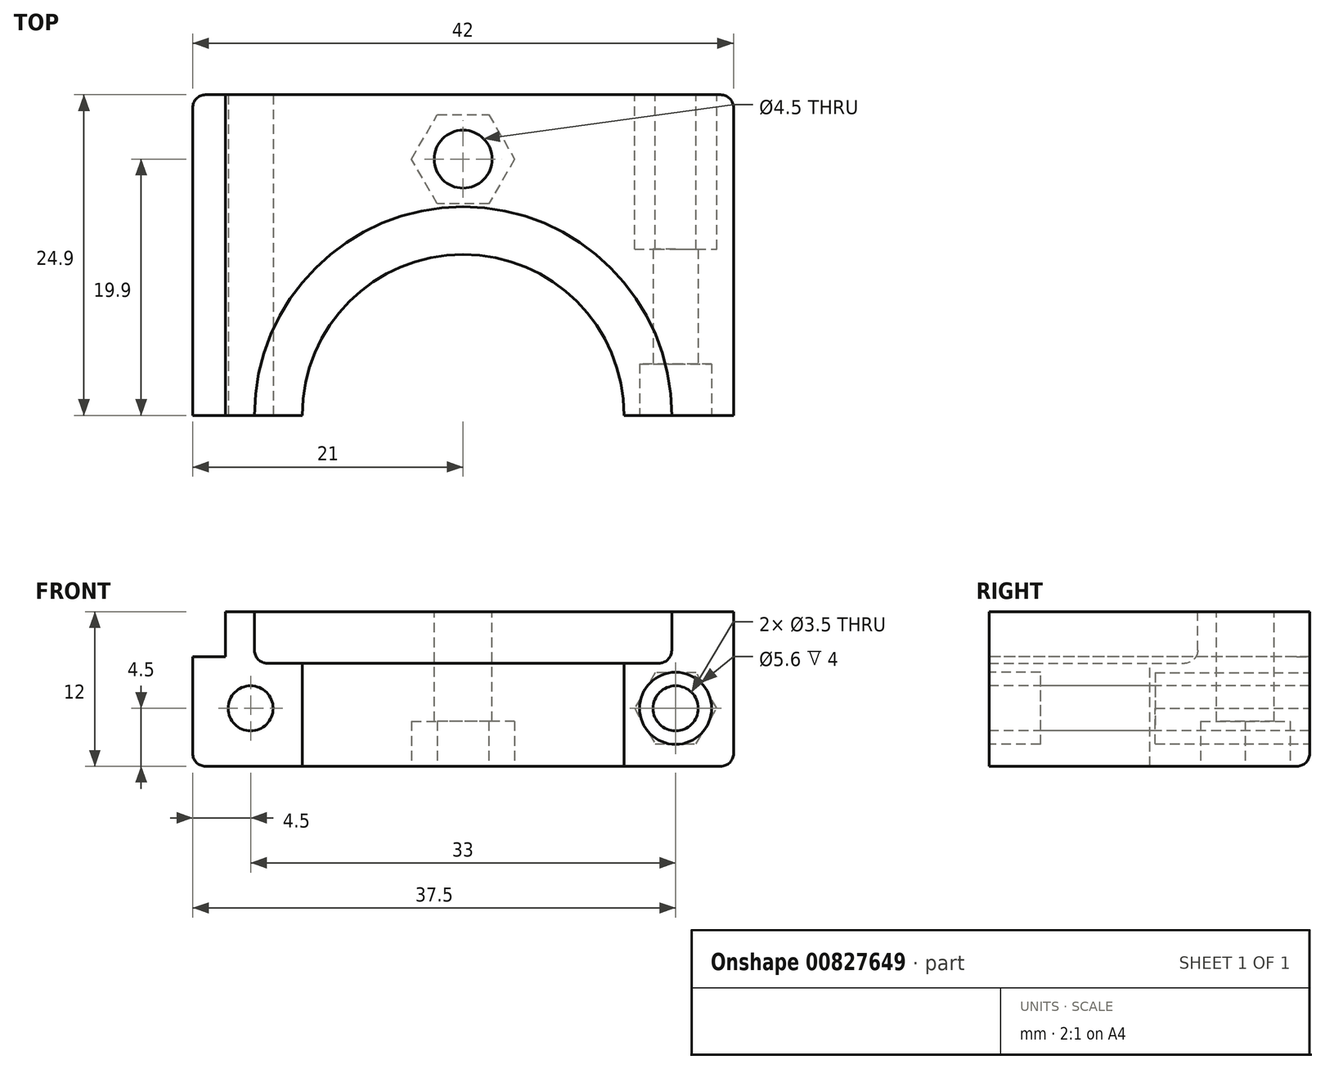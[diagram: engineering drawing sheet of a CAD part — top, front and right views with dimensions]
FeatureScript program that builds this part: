
annotation { "Feature Type Name" : "Feature", "Feature Type Description" : "" }
export const myFeature = defineFeature(function(context is Context, id is Id, definition is map)
    precondition{}
    {
        {
            var Q0;
            Q0=qCreatedBy(makeId("Top.planeOp"),FACE);
            var sketch = newSketch(context, id + "F0", { "sketchPlane" : qUnion([Q0])});
            skLineSegment(sketch, "E0.bottom", {"start": v(-21, 0) * mm, "end": v(21, 0) * mm});
            skLineSegment(sketch, "E0.top", {"start": v(-21, 24.9) * mm, "end": v(21, 24.9) * mm});
            skLineSegment(sketch, "E0.left", {"start": v(-21, 0) * mm, "end": v(-21, 24.9) * mm});
            skLineSegment(sketch, "E0.right", {"start": v(21, 0) * mm, "end": v(21, 24.9) * mm});
            skSolve(sketch);
        }
        {
            var Q0;
            Q0=makeQuery(id+"F0.imprint","IMPRINT",FACE,{"disambiguationData":[TD([[makeQuery(id+"F0.imprint","IMPRINT",EDGE,{"derivedFrom":sQuery(id+"F0.wireOp",EDGE,"E0.bottom")}),1.0]])]});
            extrude(context, id + "F1", {"entities" : qUnion([Q0]), "depth" : 12 * mm, "offsetDistance" : 25 * mm});
        }
        {
            var Q0;
            Q0=makeQuery(id+"F1.opExtrude","CAP_FACE",FACE,{"disambiguationData":[OSD([sQuery(id+"F0.wireOp",EDGE,"E0.bottom"),sQuery(id+"F0.wireOp",EDGE,"E0.top"),sQuery(id+"F0.wireOp",EDGE,"E0.left"),sQuery(id+"F0.wireOp",EDGE,"E0.right")])],"isStart":false});
            var sketch = newSketch(context, id + "F2", { "sketchPlane" : qUnion([Q0])});
            skArc(sketch, "E1", {"start": v(16.2, 0) * mm, "mid": v(0, 16.2) * mm, "end": v(-16.2, 0) * mm});
            skLineSegment(sketch, "E2", {"start": v(-16.2, 0) * mm, "end": v(16.2, 0) * mm});
            skSolve(sketch);
        }
        {
            var Q0;
            Q0=makeQuery(id+"F2.imprint","IMPRINT",FACE,{"disambiguationData":[TD([[makeQuery(id+"F2.imprint","IMPRINT",EDGE,{"derivedFrom":sQuery(id+"F2.wireOp",EDGE,"E1")}),1.0]])]});
            extrude(context, id + "F3", {"entities" : qUnion([Q0]), "operationType" : NewBodyOperationType.REMOVE, "oppositeDirection" : true, "depth" : 4 * mm, "offsetDistance" : 25 * mm});
        }
        {
            var Q0;
            Q0=makeQuery(id+"F3.boolean.opBoolean","COPY",FACE,{"derivedFrom":makeQuery(id+"F3.opExtrude","CAP_FACE",FACE,{"disambiguationData":[OSD([sQuery(id+"F2.wireOp",EDGE,"E1"),sQuery(id+"F2.wireOp",EDGE,"E2")])],"isStart":false})});
            var sketch = newSketch(context, id + "F4", { "sketchPlane" : qUnion([Q0])});
            skArc(sketch, "E3", {"start": v(12.5, 0) * mm, "mid": v(0, 12.5) * mm, "end": v(-12.5, 0) * mm});
            skLineSegment(sketch, "E4", {"start": v(-12.5, 0) * mm, "end": v(12.5, 0) * mm});
            skSolve(sketch);
        }
        {
            var Q0;
            Q0=makeQuery(id+"F4.imprint","IMPRINT",FACE,{"disambiguationData":[TD([[makeQuery(id+"F4.imprint","IMPRINT",EDGE,{"derivedFrom":sQuery(id+"F4.wireOp",EDGE,"E3")}),1.0]])]});
            extrude(context, id + "F5", {"entities" : qUnion([Q0]), "operationType" : NewBodyOperationType.REMOVE, "endBound" : BoundingType.UP_TO_NEXT, "oppositeDirection" : true, "depth" : 25 * mm, "offsetDistance" : 25 * mm});
        }
        {
            var Q0;
            Q0=makeQuery(id+"F1.opExtrude","CAP_FACE",FACE,{"disambiguationData":[OSD([sQuery(id+"F0.wireOp",EDGE,"E0.bottom"),sQuery(id+"F0.wireOp",EDGE,"E0.top"),sQuery(id+"F0.wireOp",EDGE,"E0.left"),sQuery(id+"F0.wireOp",EDGE,"E0.right")])],"isStart":false});
            var sketch = newSketch(context, id + "F6", { "sketchPlane" : qUnion([Q0])});
            skPoint(sketch, "E5", {"position": v(0, 19.9) * mm});
            skSolve(sketch);
        }
        {
            var Q0;
            Q0=sQuery(id+"F6.wireOp",VERTEX,"E5");
            var Q1;
            Q1=makeQuery(id+"F1.opExtrude","SWEPT_BODY",BODY,{"disambiguationData":[OSD([sQuery(id+"F0.wireOp",EDGE,"E0.bottom"),sQuery(id+"F0.wireOp",EDGE,"E0.top"),sQuery(id+"F0.wireOp",EDGE,"E0.left"),sQuery(id+"F0.wireOp",EDGE,"E0.right")])]});
            hole(context, id + "F7", {"style" : HoleStyle.SIMPLE, "endStyle" : HoleEndStyle.THROUGH, "holeDiameter" : 4.5 * mm, "majorDiameter" : 4 * mm, "isTappedThrough" : true, "tappedDepth" : 12 * mm, "tapClearance" : 3, "locations" : qUnion([Q0]), "scope" : qUnion([Q1])});
        }
        {
            var Q0;
            {var subQ1=sQuery(id+"F0.wireOp",EDGE,"E0.left");var subQ4=sQuery(id+"F0.wireOp",EDGE,"E0.bottom");Q0=makeQuery(id+"F5.boolean.opBoolean","SPLIT",FACE,{"disambiguationData":[TD([makeQuery(id+"F1.opExtrude","SWEPT_FACE",FACE,{"disambiguationData":[OSD([subQ1])]})])],"derivedFrom":makeQuery(id+"F1.opExtrude","SWEPT_FACE",FACE,{"disambiguationData":[OSD([subQ4])]})});}
            var sketch = newSketch(context, id + "F8", { "sketchPlane" : qUnion([Q0])});
            skLineSegment(sketch, "E6.bottom", {"start": v(-21, 12) * mm, "end": v(-18.45, 12) * mm});
            skLineSegment(sketch, "E6.top", {"start": v(-21, 8.5) * mm, "end": v(-18.45, 8.5) * mm});
            skLineSegment(sketch, "E6.left", {"start": v(-21, 12) * mm, "end": v(-21, 8.5) * mm});
            skLineSegment(sketch, "E6.right", {"start": v(-18.45, 12) * mm, "end": v(-18.45, 8.5) * mm});
            skSolve(sketch);
        }
        {
            var Q0;
            Q0=makeQuery(id+"F8.imprint","IMPRINT",FACE,{"disambiguationData":[TD([[makeQuery(id+"F8.imprint","IMPRINT",EDGE,{"derivedFrom":sQuery(id+"F8.wireOp",EDGE,"E6.bottom")}),-1.0]])]});
            extrude(context, id + "F9", {"entities" : qUnion([Q0]), "operationType" : NewBodyOperationType.REMOVE, "endBound" : BoundingType.UP_TO_NEXT, "oppositeDirection" : true, "depth" : 25 * mm, "offsetDistance" : 25 * mm});
        }
        {
            var Q0;
            Q0=qCreatedBy(makeId("Right.planeOp"),FACE);
            cPlane(context, id + "F10", {"entities" : qUnion([Q0]), "cplaneType" : CPlaneType.OFFSET, "offset" : 0 * mm, "width" : 150 * mm, "height" : 150 * mm});
        }
        {
            var Q0;
            {var subQ1=sQuery(id+"F0.wireOp",EDGE,"E0.left");var subQ4=sQuery(id+"F0.wireOp",EDGE,"E0.bottom");Q0=makeQuery(id+"F5.boolean.opBoolean","SPLIT",FACE,{"disambiguationData":[TD([makeQuery(id+"F1.opExtrude","SWEPT_FACE",FACE,{"disambiguationData":[OSD([subQ1])]})])],"derivedFrom":makeQuery(id+"F1.opExtrude","SWEPT_FACE",FACE,{"disambiguationData":[OSD([subQ4])]})});}
            var sketch = newSketch(context, id + "F11", { "sketchPlane" : qUnion([Q0])});
            skPoint(sketch, "E7", {"position": v(-16.5, 4.5) * mm});
            skPoint(sketch, "E8", {"position": v(16.5, 4.5) * mm});
            skSolve(sketch);
        }
        {
            var Q0;
            Q0=sQuery(id+"F11.wireOp",VERTEX,"E7");
            var Q1;
            Q1=sQuery(id+"F11.wireOp",VERTEX,"E8");
            var Q2;
            Q2=makeQuery(id+"F1.opExtrude","SWEPT_BODY",BODY,{"disambiguationData":[OSD([sQuery(id+"F0.wireOp",EDGE,"E0.bottom"),sQuery(id+"F0.wireOp",EDGE,"E0.top"),sQuery(id+"F0.wireOp",EDGE,"E0.left"),sQuery(id+"F0.wireOp",EDGE,"E0.right")])]});
            hole(context, id + "F12", {"style" : HoleStyle.SIMPLE, "endStyle" : HoleEndStyle.THROUGH, "holeDiameter" : 3.5 * mm, "majorDiameter" : 3 * mm, "isTappedThrough" : true, "tappedDepth" : 13.5 * mm, "tapClearance" : 3, "locations" : qUnion([Q0, Q1]), "scope" : qUnion([Q2])});
        }
        {
            var Q0;
            Q0=makeQuery(id+"F0.imprint","IMPRINT",FACE,{"disambiguationData":[TD([[makeQuery(id+"F0.imprint","IMPRINT",EDGE,{"derivedFrom":sQuery(id+"F0.wireOp",EDGE,"E0.bottom")}),1.0]])]});
            var sketch = newSketch(context, id + "F13", { "sketchPlane" : qUnion([Q0])});
            skCircle(sketch, "E9.cCircle", {"center": v(0, 19.9) * mm, "radius": 3.46 * mm, "construction": true});
            skLineSegment(sketch, "E9.0", {"start": v(-4, 19.9) * mm, "end": v(-2, 23.36) * mm});
            skLineSegment(sketch, "E9.1", {"start": v(-2, 23.37) * mm, "end": v(2, 23.37) * mm});
            skLineSegment(sketch, "E9.2", {"start": v(2, 23.37) * mm, "end": v(4, 19.9) * mm});
            skLineSegment(sketch, "E9.3", {"start": v(4, 19.9) * mm, "end": v(2, 16.44) * mm});
            skLineSegment(sketch, "E9.4", {"start": v(2, 16.44) * mm, "end": v(-2, 16.44) * mm});
            skLineSegment(sketch, "E9.5", {"start": v(-2, 16.44) * mm, "end": v(-4, 19.9) * mm});
            skPoint(sketch, "E9.0.midPoint", {"position": v(-3, 21.63) * mm});
            skSolve(sketch);
        }
        {
            var Q0;
            Q0=makeQuery(id+"F13.imprint","IMPRINT",FACE,{"disambiguationData":[TD([[makeQuery(id+"F13.imprint","IMPRINT",EDGE,{"derivedFrom":sQuery(id+"F13.wireOp",EDGE,"E9.0")}),-1.0]])]});
            extrude(context, id + "F14", {"entities" : qUnion([Q0]), "operationType" : NewBodyOperationType.REMOVE, "depth" : 3.5 * mm, "offsetDistance" : 25 * mm});
        }
        {
            var Q0;
            {var subQ1=sQuery(id+"F0.wireOp",EDGE,"E0.right");var subQ4=sQuery(id+"F0.wireOp",EDGE,"E0.bottom");Q0=makeQuery(id+"F5.boolean.opBoolean","SPLIT",FACE,{"disambiguationData":[TD([makeQuery(id+"F1.opExtrude","SWEPT_FACE",FACE,{"disambiguationData":[OSD([subQ1])]})])],"derivedFrom":makeQuery(id+"F1.opExtrude","SWEPT_FACE",FACE,{"disambiguationData":[OSD([subQ4])]})});}
            var sketch = newSketch(context, id + "F15", { "sketchPlane" : qUnion([Q0])});
            skCircle(sketch, "E10", {"center": v(16.5, 4.5) * mm, "radius": 2.8 * mm});
            skCircle(sketch, "E11", {"center": v(16.5, 4.5) * mm, "radius": 1.75 * mm});
            skSolve(sketch);
        }
        {
            var Q0;
            Q0=makeQuery(id+"F15.imprint","IMPRINT",FACE,{"disambiguationData":[TD([[makeQuery(id+"F15.imprint","IMPRINT",EDGE,{"derivedFrom":sQuery(id+"F15.wireOp",EDGE,"E10")}),1.0]])]});
            extrude(context, id + "F16", {"entities" : qUnion([Q0]), "operationType" : NewBodyOperationType.REMOVE, "oppositeDirection" : true, "depth" : 4 * mm, "offsetDistance" : 25 * mm});
        }
        {
            var Q0;
            Q0=makeQuery(id+"F1.opExtrude","SWEPT_FACE",FACE,{"disambiguationData":[OSD([sQuery(id+"F0.wireOp",EDGE,"E0.top")])]});
            var sketch = newSketch(context, id + "F17", { "sketchPlane" : qUnion([Q0])});
            skCircle(sketch, "E12.cCircle", {"center": v(-16.5, 4.5) * mm, "radius": 2.77 * mm, "construction": true});
            skLineSegment(sketch, "E12.0", {"start": v(-18.1, 1.74) * mm, "end": v(-19.7, 4.5) * mm});
            skLineSegment(sketch, "E12.1", {"start": v(-19.7, 4.5) * mm, "end": v(-18.1, 7.27) * mm});
            skLineSegment(sketch, "E12.2", {"start": v(-18.1, 7.27) * mm, "end": v(-14.9, 7.27) * mm});
            skLineSegment(sketch, "E12.3", {"start": v(-14.9, 7.27) * mm, "end": v(-13.3, 4.5) * mm});
            skLineSegment(sketch, "E12.4", {"start": v(-13.3, 4.5) * mm, "end": v(-14.9, 1.74) * mm});
            skLineSegment(sketch, "E12.5", {"start": v(-14.9, 1.74) * mm, "end": v(-18.1, 1.74) * mm});
            skPoint(sketch, "E12.0.midPoint", {"position": v(-18.9, 3.12) * mm});
            skSolve(sketch);
        }
        {
            var Q0;
            Q0=makeQuery(id+"F17.imprint","IMPRINT",FACE,{"disambiguationData":[TD([[makeQuery(id+"F17.imprint","IMPRINT",EDGE,{"derivedFrom":sQuery(id+"F17.wireOp",EDGE,"E12.0")}),-1.0]])]});
            extrude(context, id + "F18", {"entities" : qUnion([Q0]), "operationType" : NewBodyOperationType.REMOVE, "oppositeDirection" : true, "depth" : 12 * mm, "offsetDistance" : 25 * mm});
        }
        {
            var Q0;
            Q0=makeQuery(id+"F1.opExtrude","SWEPT_EDGE",EDGE,{"disambiguationData":[OSD([sQuery(id+"F0.wireOp",EDGE,"E0.top"),sQuery(id+"F0.wireOp",EDGE,"E0.right")])]});
            var Q1;
            Q1=makeQuery(id+"F1.opExtrude","CAP_EDGE",EDGE,{"disambiguationData":[OSD([sQuery(id+"F0.wireOp",EDGE,"E0.top")])],"isStart":true});
            var Q2;
            Q2=makeQuery(id+"F1.opExtrude","SWEPT_EDGE",EDGE,{"disambiguationData":[OSD([sQuery(id+"F0.wireOp",EDGE,"E0.top"),sQuery(id+"F0.wireOp",EDGE,"E0.left")])]});
            var Q3;
            Q3=makeQuery(id+"F1.opExtrude","CAP_EDGE",EDGE,{"disambiguationData":[OSD([sQuery(id+"F0.wireOp",EDGE,"E0.left")])],"isStart":true});
            var Q4;
            Q4=makeQuery(id+"F1.opExtrude","CAP_EDGE",EDGE,{"disambiguationData":[OSD([sQuery(id+"F0.wireOp",EDGE,"E0.right")])],"isStart":true});
            var Q5;
            Q5=makeQuery(id+"F5.boolean.opBoolean","COPY",EDGE,{"derivedFrom":makeQuery(id+"F5.opExtrude","TWEAK_EDGE",EDGE,{"derivedFrom":[makeQuery(id+"F1.opExtrude","CAP_FACE",FACE,{"disambiguationData":[OSD([sQuery(id+"F0.wireOp",EDGE,"E0.bottom"),sQuery(id+"F0.wireOp",EDGE,"E0.top"),sQuery(id+"F0.wireOp",EDGE,"E0.left"),sQuery(id+"F0.wireOp",EDGE,"E0.right")])],"isStart":true}),makeQuery(id+"F4.imprint","IMPRINT",EDGE,{"derivedFrom":sQuery(id+"F4.wireOp",EDGE,"E3")})]})});
            var Q6;
            Q6=makeQuery(id+"F5.boolean.opBoolean","COPY",EDGE,{"derivedFrom":makeQuery(id+"F5.opExtrude","CAP_EDGE",EDGE,{"disambiguationData":[OSD([sQuery(id+"F4.wireOp",EDGE,"E3")])],"isStart":true})});
            var Q7;
            Q7=makeQuery(id+"F3.boolean.opBoolean","COPY",EDGE,{"derivedFrom":makeQuery(id+"F3.opExtrude","CAP_EDGE",EDGE,{"disambiguationData":[OSD([sQuery(id+"F2.wireOp",EDGE,"E1")])],"isStart":false})});
            fillet(context, id + "F19", {"entities" : qUnion([Q0, Q1, Q2, Q3, Q4, Q5, Q6, Q7]), "radius" : 1 * mm, "tangentPropagation" : true, "allowEdgeOverflow" : false});
        }
    });
